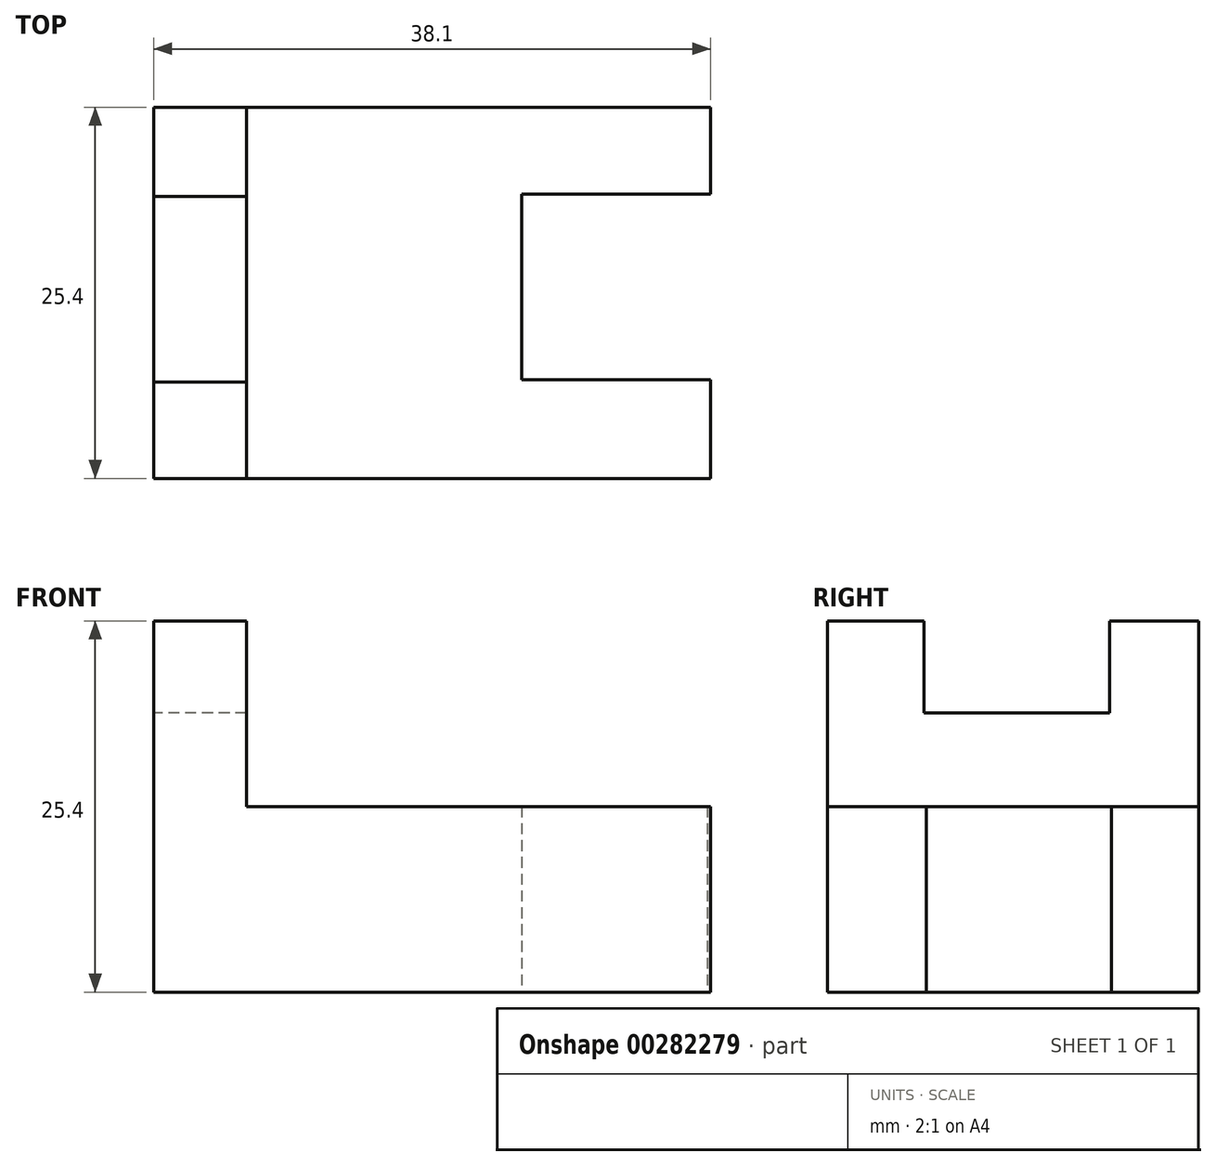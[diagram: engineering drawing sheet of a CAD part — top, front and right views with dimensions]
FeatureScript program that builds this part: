
annotation { "Feature Type Name" : "Feature", "Feature Type Description" : "" }
export const myFeature = defineFeature(function(context is Context, id is Id, definition is map)
    precondition{}
    {
        {
            var Q0;
            Q0=qCreatedBy(makeId("Front.planeOp"),FACE);
            var sketch = newSketch(context, id + "F0", { "sketchPlane" : qUnion([Q0])});
            skLineSegment(sketch, "E0", {"start": v(0, 0) * mm, "end": v(0, 25.4) * mm});
            skLineSegment(sketch, "E1", {"start": v(0, 25.4) * mm, "end": v(6.35, 25.4) * mm});
            skLineSegment(sketch, "E2", {"start": v(6.35, 25.4) * mm, "end": v(6.35, 12.7) * mm});
            skLineSegment(sketch, "E3", {"start": v(6.35, 12.7) * mm, "end": v(38.1, 12.7) * mm});
            skLineSegment(sketch, "E4", {"start": v(38.1, 12.7) * mm, "end": v(38.1, 0) * mm});
            skLineSegment(sketch, "E5", {"start": v(38.1, 0) * mm, "end": v(0, 0) * mm});
            skSolve(sketch);
        }
        {
            var Q0;
            Q0=makeQuery(id+"F0.imprint","IMPRINT",FACE,{"disambiguationData":[TD([[makeQuery(id+"F0.imprint","IMPRINT",EDGE,{"derivedFrom":sQuery(id+"F0.wireOp",EDGE,"E0")}),-1.0]])]});
            extrude(context, id + "F1", {"entities" : qUnion([Q0]), "depth" : 25.4 * mm});
        }
        {
            var Q0;
            Q0=qCreatedBy(makeId("Right.planeOp"),FACE);
            var sketch = newSketch(context, id + "F2", { "sketchPlane" : qUnion([Q0])});
            skLineSegment(sketch, "E6", {"start": v(-18.8, 25.44) * mm, "end": v(-18.8, 19.09) * mm});
            skLineSegment(sketch, "E7", {"start": v(-18.8, 19.09) * mm, "end": v(-6.1, 19.09) * mm});
            skLineSegment(sketch, "E8", {"start": v(-6.1, 19.09) * mm, "end": v(-6.1, 25.44) * mm});
            skLineSegment(sketch, "E9", {"start": v(-6.1, 25.44) * mm, "end": v(-18.8, 25.44) * mm});
            skSolve(sketch);
        }
        {
            var Q0;
            Q0 = qSketchRegion(id + "F2", true);
            extrude(context, id + "F3", {"entities" : qUnion([Q0]), "operationType" : NewBodyOperationType.REMOVE, "depth" : 25.4 * mm});
        }
        {
            var Q0;
            Q0=qCreatedBy(makeId("Top.planeOp"),FACE);
            var sketch = newSketch(context, id + "F4", { "sketchPlane" : qUnion([Q0])});
            skLineSegment(sketch, "E10", {"start": v(37.88, -5.95) * mm, "end": v(25.18, -5.95) * mm});
            skLineSegment(sketch, "E11", {"start": v(25.18, -5.95) * mm, "end": v(25.18, -18.65) * mm});
            skLineSegment(sketch, "E12", {"start": v(25.18, -18.65) * mm, "end": v(37.88, -18.65) * mm});
            skLineSegment(sketch, "E13", {"start": v(37.88, -5.95) * mm, "end": v(47.87, -5.95) * mm});
            skLineSegment(sketch, "E14", {"start": v(47.87, -5.95) * mm, "end": v(47.87, -18.5) * mm});
            skLineSegment(sketch, "E15", {"start": v(47.87, -18.5) * mm, "end": v(37.88, -18.65) * mm});
            skSolve(sketch);
        }
        {
            var Q0;
            Q0 = qSketchRegion(id + "F4", true);
            extrude(context, id + "F5", {"entities" : qUnion([Q0]), "operationType" : NewBodyOperationType.REMOVE, "depth" : 25.4 * mm});
        }
    });
